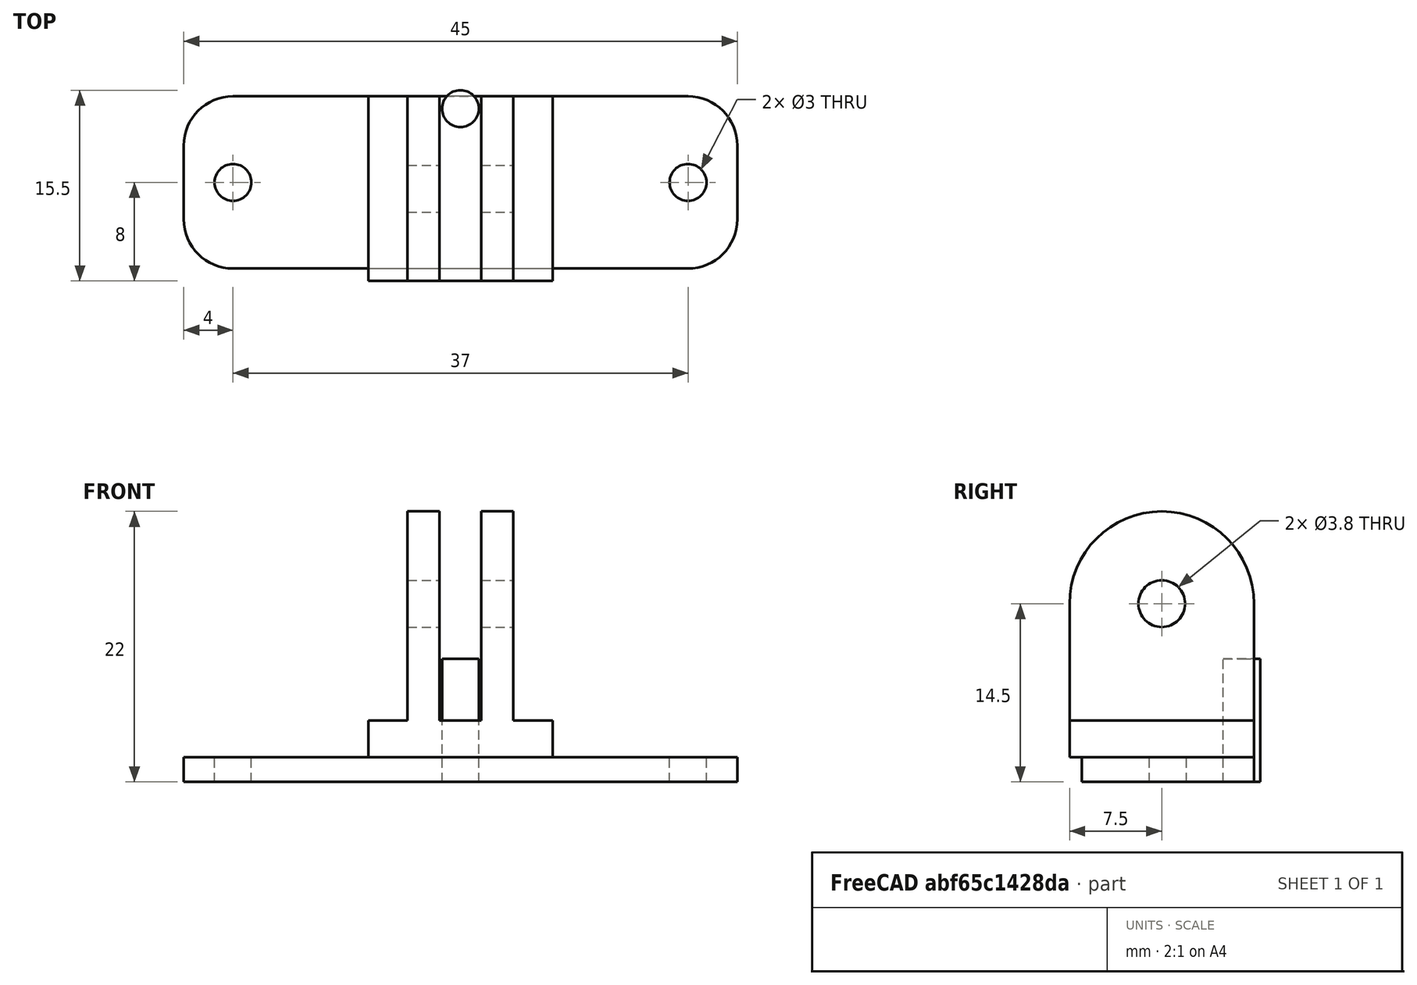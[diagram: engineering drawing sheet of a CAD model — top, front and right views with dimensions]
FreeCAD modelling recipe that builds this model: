
FCSTD DOCUMENT  (FreeCAD 0.19R23578 (Git))
Label: sharp_2y0a02
License: FreeArt
LicenseURL: http://artlibre.org/licence/lal
objects: Part::Box×1, Spreadsheet::Sheet×1, Part::Feature×1, Part::Cylinder×1, Part::FeaturePython×1, Part::Fillet×1, Part::MultiFuse×1, Part::Cut×1, App::Part×1
note: 6 computed .brp shape members not serialized (recipe doc carries the construction recipe); baked Part::Feature solids carry a one-line shape summary decoded from their .brp

FEATURE [Part::Box] Box008  label="sensor holder cube"
  AttacherType = Attacher::AttachEngine3D
  Height = 2
  Length = 45
  Placement = pos=(-22.5,-6.5,0) rot=(0,0,1;0rad)
  Width = 14
  expr: .Placement.Base.y = 15 / 2 - <<p>>.sensor_holder_y
  expr: .Placement.Base.x = -<<p>>.sensor_holder_x / 2
  expr: Width = <<p>>.sensor_holder_y
  expr: Height = <<p>>.sensor_holder_z
  expr: Length = <<p>>.sensor_holder_x
FEATURE [Spreadsheet::Sheet] Spreadsheet001  label="p"
  cells = A1=sensor_holder_x; B1(sensor_holder_x)=45; A2=sensor_holder_y; B2(sensor_holder_y)=14; A3=sensor_holder_z; B3(sensor_holder_z)=2; A4=hole_dist_x; B4(hole_dist_x)=37; A5=hole_r; B5(hole_r)=1.5
FEATURE [Part::Feature] Cut001001  label="side 2 cut"
  Placement = pos=(0,0,2) rot=(0,0,1;1.5708rad)
  shape: bbox 15 x 15 x 20 mm, 16 faces (baked)
  expr: .Placement.Base.z = <<p>>.sensor_holder_z
FEATURE [Part::Cylinder] Cylinder001  label="screw hole"
  Angle = 360
  AttacherType = Attacher::AttachEngine3D
  Height = 10
  Placement = pos=(0,6.5,0) rot=(0,0,1;0rad)
  Radius = 1.5
  expr: .Placement.Base.y = <<p>>.sensor_holder_y - 15 / 2
  expr: Radius = <<p>>.hole_r
FEATURE [Part::FeaturePython] Array  label="screw hole array"  # Draft array (typed FeaturePython)
  Angle = 360
  ArrayType = 0
  Axis = (0,0,1)
  Base = -> Cylinder001
  Center = (0,0,0)
  Count = 2
  ExpandArray = false
  Fuse = false
  IntervalAxis = (0,0,0)
  IntervalX = (37,0,0)
  IntervalY = (0,100,0)
  IntervalZ = (0,0,100)
  NumberCircles = 3
  NumberPolar = 5
  NumberX = 2
  NumberY = 1
  NumberZ = 1
  Placement = pos=(-18.5,-6,0) rot=(0,0,1;0rad)
  PlacementList = 2 placements: [(0,6.5,0),(37,6.5,0)]
  RadialDistance = 50
  ScaleList = (2) [(1,1,1),(1,1,1)]
  Symmetry = 1
  TangentialDistance = 25
  expr: .Placement.Base.y = -<<p>>.sensor_holder_y / 2 + 15 - <<p>>.sensor_holder_y
  expr: .Placement.Base.x = -<<p>>.hole_dist_x / 2
  expr: .IntervalX.x = <<p>>.hole_dist_x
FEATURE [Part::Fillet] Fillet  label="sensor holder fillet"
  Base = -> Box008
  Edges = 4 edges r=4: [Edge1,Edge3,Edge5,Edge7]
FEATURE [Part::MultiFuse] Fusion  label="body fusion"
  Shapes = -> [Cut001001,Fillet]
FEATURE [Part::Cut] Cut001002  label="body cut"
  Base = -> Fusion
  Tool = -> Array
FEATURE [App::Part] Part  label="pcb box part"
  Group = -> [Cut001001,Fusion,Cut001002]
  Origin = -> Origin
